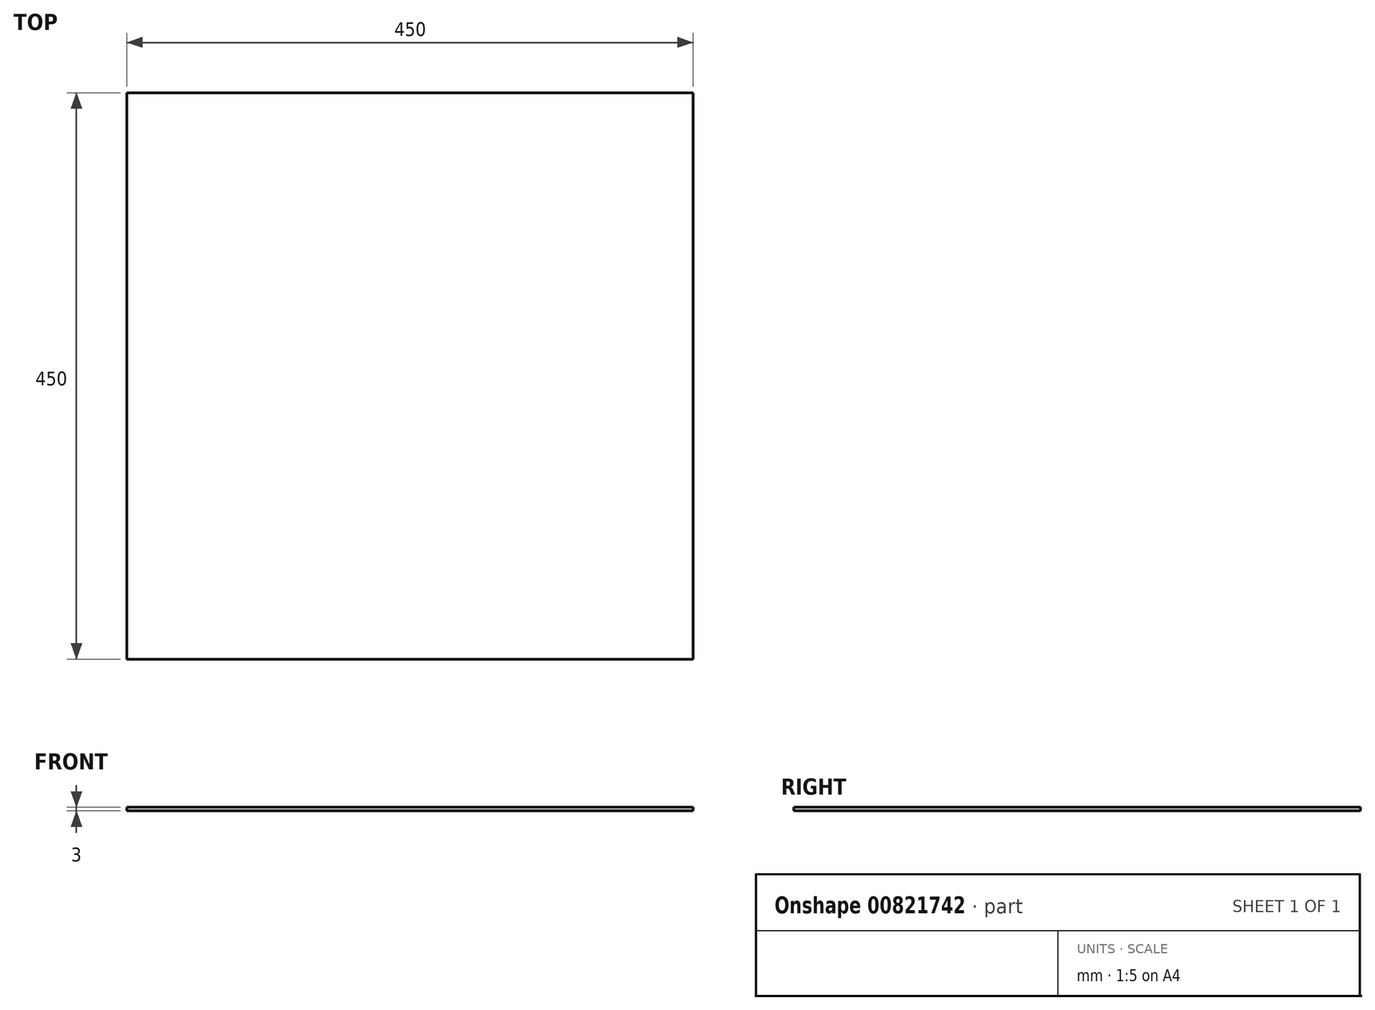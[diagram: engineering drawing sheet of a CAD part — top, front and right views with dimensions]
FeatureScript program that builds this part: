
annotation { "Feature Type Name" : "Feature", "Feature Type Description" : "" }
export const myFeature = defineFeature(function(context is Context, id is Id, definition is map)
    precondition{}
    {
        {
            var Q0;
            Q0=qCreatedBy(makeId("Top.planeOp"),FACE);
            var sketch = newSketch(context, id + "F0", { "sketchPlane" : qUnion([Q0])});
            skLineSegment(sketch, "E0.bottom", {"start": v(-225, -225) * mm, "end": v(225, -225) * mm});
            skLineSegment(sketch, "E0.top", {"start": v(-225, 225) * mm, "end": v(225, 225) * mm});
            skLineSegment(sketch, "E0.left", {"start": v(-225, -225) * mm, "end": v(-225, 225) * mm});
            skLineSegment(sketch, "E0.right", {"start": v(225, -225) * mm, "end": v(225, 225) * mm});
            skPoint(sketch, "E0.middle", {"position": v(0, 0) * mm});
            skSolve(sketch);
        }
        {
            var Q0;
            Q0 = qSketchRegion(id + "F0", true);
            extrude(context, id + "F1", {"entities" : qUnion([Q0]), "depth" : 3 * mm, "offsetDistance" : 25 * mm});
        }
    });
